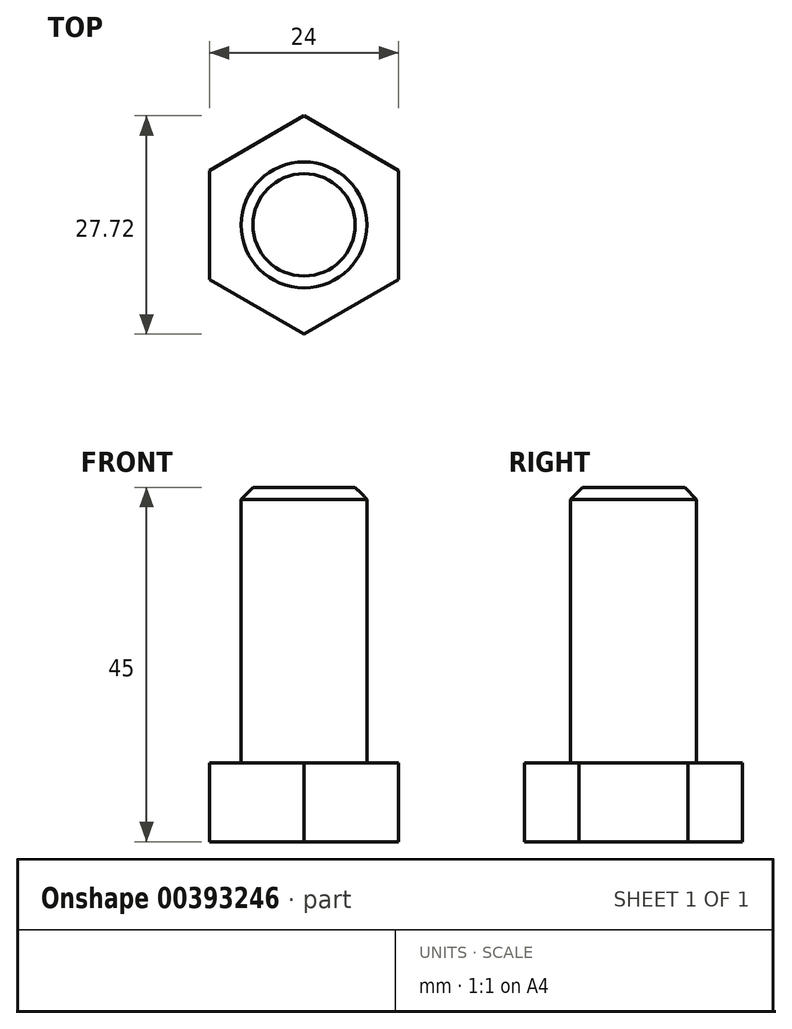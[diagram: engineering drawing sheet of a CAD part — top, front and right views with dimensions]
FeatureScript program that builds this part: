
annotation { "Feature Type Name" : "Feature", "Feature Type Description" : "" }
export const myFeature = defineFeature(function(context is Context, id is Id, definition is map)
    precondition{}
    {
        {
            var Q0;
            Q0=qCreatedBy(makeId("Top.planeOp"),FACE);
            var sketch = newSketch(context, id + "F0", { "sketchPlane" : qUnion([Q0])});
            skCircle(sketch, "E0.cCircle", {"center": v(0, 0) * mm, "radius": 12 * mm, "construction": true});
            skLineSegment(sketch, "E0.0", {"start": v(12, 6.93) * mm, "end": v(12, -6.93) * mm});
            skLineSegment(sketch, "E0.1", {"start": v(12, -6.93) * mm, "end": v(0, -13.86) * mm});
            skLineSegment(sketch, "E0.2", {"start": v(0, -13.86) * mm, "end": v(-12, -6.93) * mm});
            skLineSegment(sketch, "E0.3", {"start": v(-12, -6.93) * mm, "end": v(-12, 6.93) * mm});
            skLineSegment(sketch, "E0.4", {"start": v(-12, 6.93) * mm, "end": v(0, 13.86) * mm});
            skLineSegment(sketch, "E0.5", {"start": v(0, 13.86) * mm, "end": v(12, 6.93) * mm});
            skPoint(sketch, "E0.0.midPoint", {"position": v(12, 0) * mm});
            skSolve(sketch);
        }
        {
            var Q0;
            Q0 = qSketchRegion(id + "F0", true);
            extrude(context, id + "F1", {"entities" : qUnion([Q0]), "depth" : 10 * mm});
        }
        {
            var Q0;
            Q0=makeQuery(id+"F1.opExtrude","CAP_FACE",FACE,{"disambiguationData":[OSD([sQuery(id+"F0.wireOp",EDGE,"E0.0"),sQuery(id+"F0.wireOp",EDGE,"E0.1"),sQuery(id+"F0.wireOp",EDGE,"E0.2"),sQuery(id+"F0.wireOp",EDGE,"E0.3"),sQuery(id+"F0.wireOp",EDGE,"E0.4"),sQuery(id+"F0.wireOp",EDGE,"E0.5")])],"isStart":false});
            var sketch = newSketch(context, id + "F2", { "sketchPlane" : qUnion([Q0])});
            skCircle(sketch, "E1", {"center": v(0, 0) * mm, "radius": 8 * mm});
            skSolve(sketch);
        }
        {
            var Q0;
            Q0 = qSketchRegion(id + "F2", true);
            extrude(context, id + "F3", {"entities" : qUnion([Q0]), "operationType" : NewBodyOperationType.ADD, "depth" : 35 * mm});
        }
        {
            var Q0;
            Q0=makeQuery(id+"F3.opExtrude","CAP_EDGE",EDGE,{"disambiguationData":[OSD([sQuery(id+"F2.wireOp",EDGE,"E1")])],"isStart":false});
            chamfer(context, id + "F4", {"entities" : qUnion([Q0]), "width" : 1.5 * mm, "tangentPropagation" : true});
        }
    });
